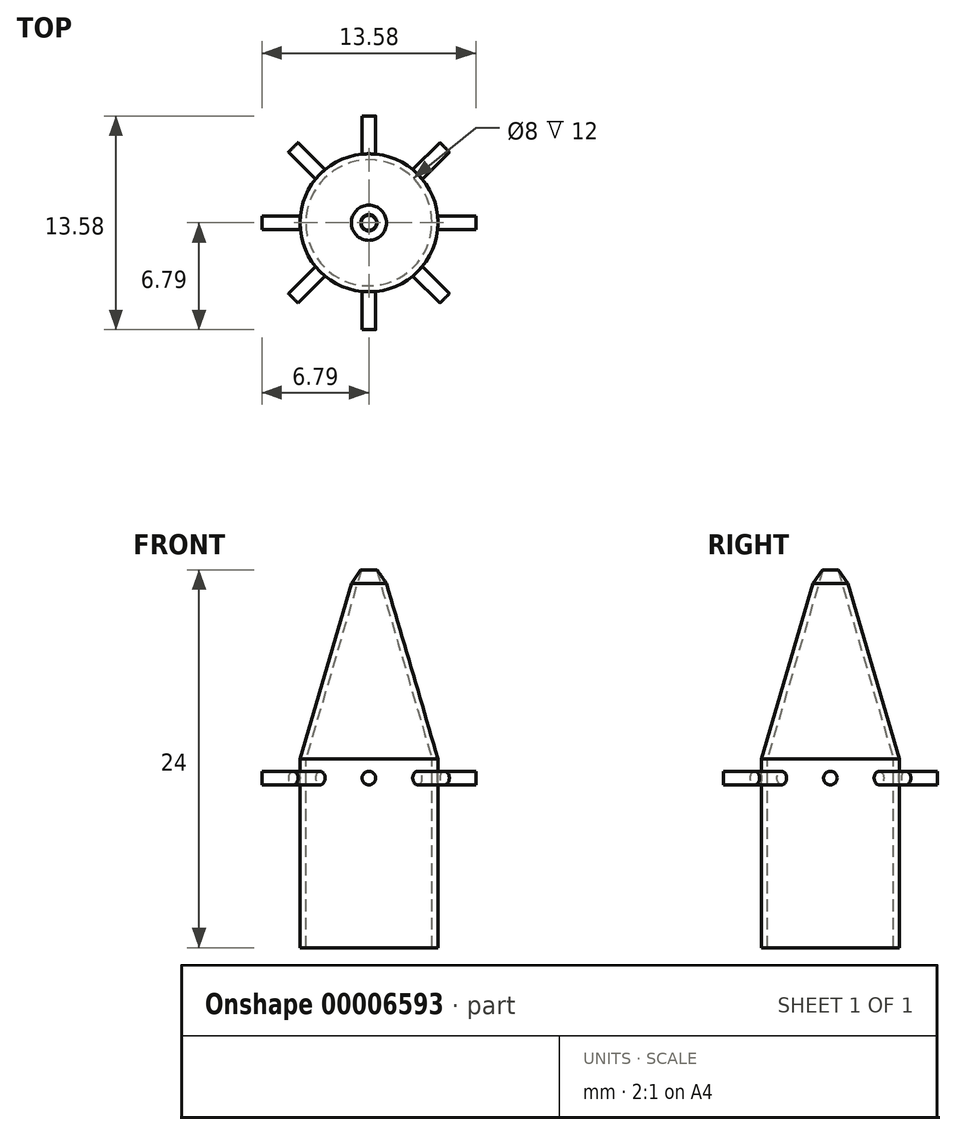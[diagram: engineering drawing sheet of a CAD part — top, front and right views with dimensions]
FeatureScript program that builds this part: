
annotation { "Feature Type Name" : "Feature", "Feature Type Description" : "" }
export const myFeature = defineFeature(function(context is Context, id is Id, definition is map)
    precondition{}
    {
        {
            var Q0;
            Q0=qCreatedBy(makeId("Front.planeOp"),FACE);
            var sketch = newSketch(context, id + "F0", { "sketchPlane" : qUnion([Q0])});
            skLineSegment(sketch, "E0", {"start": v(0, 0) * mm, "end": v(0.48, 0) * mm});
            skLineSegment(sketch, "E1", {"start": v(0.48, 0) * mm, "end": v(0.52, 0) * mm});
            skLineSegment(sketch, "E2", {"start": v(0, 0) * mm, "end": v(0, -12) * mm});
            skLineSegment(sketch, "E3", {"start": v(0, -12) * mm, "end": v(4, -12) * mm});
            skLineSegment(sketch, "E4", {"start": v(0.48, 0) * mm, "end": v(4, -12) * mm});
            skLineSegment(sketch, "E5", {"start": v(0.52, 0) * mm, "end": v(1.12, -0.87) * mm});
            skLineSegment(sketch, "E6", {"start": v(1.12, -0.87) * mm, "end": v(4.38, -12) * mm});
            skLineSegment(sketch, "E7", {"start": v(4.38, -12) * mm, "end": v(4, -12) * mm});
            skLineSegment(sketch, "E8", {"start": v(4, -12) * mm, "end": v(4, -24) * mm});
            skLineSegment(sketch, "E9", {"start": v(4, -24) * mm, "end": v(4.38, -24) * mm});
            skLineSegment(sketch, "E10", {"start": v(4.38, -24) * mm, "end": v(4.38, -12) * mm});
            skLineSegment(sketch, "E11", {"start": v(6.8, -12.8) * mm, "end": v(6.8, -13.23) * mm});
            skLineSegment(sketch, "E12", {"start": v(6.8, -13.23) * mm, "end": v(5.64, -13.23) * mm});
            skSolve(sketch);
        }
        {
            var Q0;
            Q0=sQuery(id+"F0.wireOp",EDGE,"E11");
            var Q1;
            Q1=sQuery(id+"F0.wireOp",EDGE,"E12");
            revolve(context, id + "F1", {"bodyType" : ToolBodyType.SURFACE, "surfaceEntities" : qUnion([Q0]), "axis" : qUnion([Q1]), "revolveType" : RevolveType.FULL});
        }
        {
            var Q0;
            Q0=makeQuery(id+"F0.imprint","IMPRINT",FACE,{"disambiguationData":[TD([[makeQuery(id+"F0.imprint","IMPRINT",EDGE,{"derivedFrom":sQuery(id+"F0.wireOp",EDGE,"E1")}),-1.0]])]});
            var Q1;
            Q1=makeQuery(id+"F0.imprint","IMPRINT",FACE,{"disambiguationData":[TD([[makeQuery(id+"F0.imprint","IMPRINT",EDGE,{"derivedFrom":sQuery(id+"F0.wireOp",EDGE,"E7")}),1.0]])]});
            var Q2;
            Q2=sQuery(id+"F0.wireOp",EDGE,"E2");
            revolve(context, id + "F2", {"entities" : qUnion([Q0, Q1]), "axis" : qUnion([Q2]), "revolveType" : RevolveType.FULL});
        }
        {
            var Q0;
            Q0=makeQuery(id+"F1.opRevolve","SWEPT_FACE",FACE,{"disambiguationData":[OSD([sQuery(id+"F0.wireOp",EDGE,"E11")])]});
            var Q1;
            Q1=makeQuery(id+"F2.opRevolve","SWEPT_BODY",BODY,{"disambiguationData":[OSD([sQuery(id+"F0.wireOp",EDGE,"E1"),sQuery(id+"F0.wireOp",EDGE,"E4"),sQuery(id+"F0.wireOp",EDGE,"E5"),sQuery(id+"F0.wireOp",EDGE,"E6"),sQuery(id+"F0.wireOp",EDGE,"E8"),sQuery(id+"F0.wireOp",EDGE,"E9"),sQuery(id+"F0.wireOp",EDGE,"E10")])]});
            extrude(context, id + "F3", {"entities" : qUnion([Q0]), "endBound" : BoundingType.UP_TO_BODY, "oppositeDirection" : true, "endBoundEntityBody" : qUnion([Q1]), "depth" : 25 * mm});
        }
        {
            var Q0;
            Q0=makeQuery(id+"F3.opExtrude","SWEPT_BODY",BODY,{"disambiguationData":[OSD([sQuery(id+"F0.wireOp",EDGE,"E11")])]});
            var Q1;
            Q1=sQuery(id+"F0.wireOp",EDGE,"E2");
            circularPattern(context, id + "F4", {"entities" : qUnion([Q0]), "axis" : qUnion([Q1]), "angle" : 360 / 8 * degree, "instanceCount" : 8});
        }
    });
